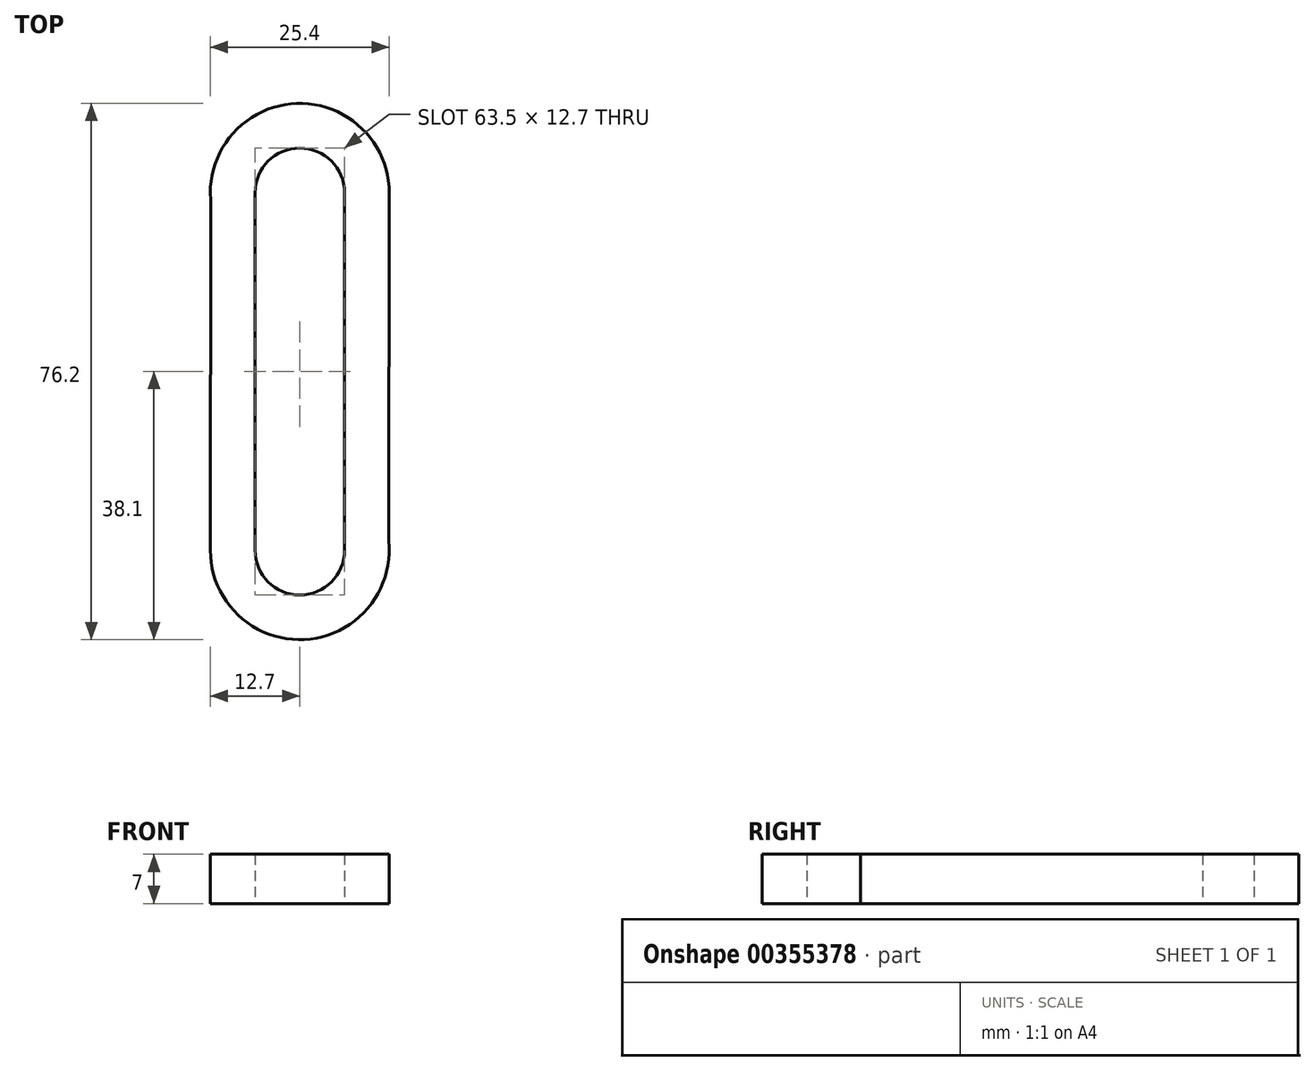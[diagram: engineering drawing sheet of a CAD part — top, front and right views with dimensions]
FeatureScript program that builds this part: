
annotation { "Feature Type Name" : "Feature", "Feature Type Description" : "" }
export const myFeature = defineFeature(function(context is Context, id is Id, definition is map)
    precondition{}
    {
        {
            var Q0;
            Q0=qCreatedBy(makeId("Top.planeOp"),FACE);
            var sketch = newSketch(context, id + "F0", { "sketchPlane" : qUnion([Q0])});
            skArc(sketch, "E0", {"start": v(6.35, 25.4) * mm, "mid": v(0, 31.75) * mm, "end": v(-6.35, 25.4) * mm});
            skArc(sketch, "E1", {"start": v(-6.35, -25.4) * mm, "mid": v(0, -31.75) * mm, "end": v(6.35, -25.4) * mm});
            skArc(sketch, "E2.0", {"start": v(12.7, 25.38) * mm, "mid": v(-0.45, 38.1) * mm, "end": v(-12.67, 24.48) * mm});
            skArc(sketch, "E3.0", {"start": v(-12.7, -25.4) * mm, "mid": v(0.65, -38.08) * mm, "end": v(12.63, -24.09) * mm});
            skLineSegment(sketch, "E4", {"start": v(-12.67, 26.34) * mm, "end": v(-12.7, -25.4) * mm});
            skLineSegment(sketch, "E5", {"start": v(12.63, -26.74) * mm, "end": v(12.7, 25.4) * mm});
            skLineSegment(sketch, "E6", {"start": v(-6.35, 25.4) * mm, "end": v(-6.35, -25.4) * mm});
            skLineSegment(sketch, "E7", {"start": v(6.35, 25.4) * mm, "end": v(6.35, -26.74) * mm});
            skSolve(sketch);
        }
        {
            var Q0;
            Q0 = qSketchRegion(id + "F0", true);
            extrude(context, id + "F1", {"entities" : qUnion([Q0]), "depth" : 7 * mm});
        }
    });
